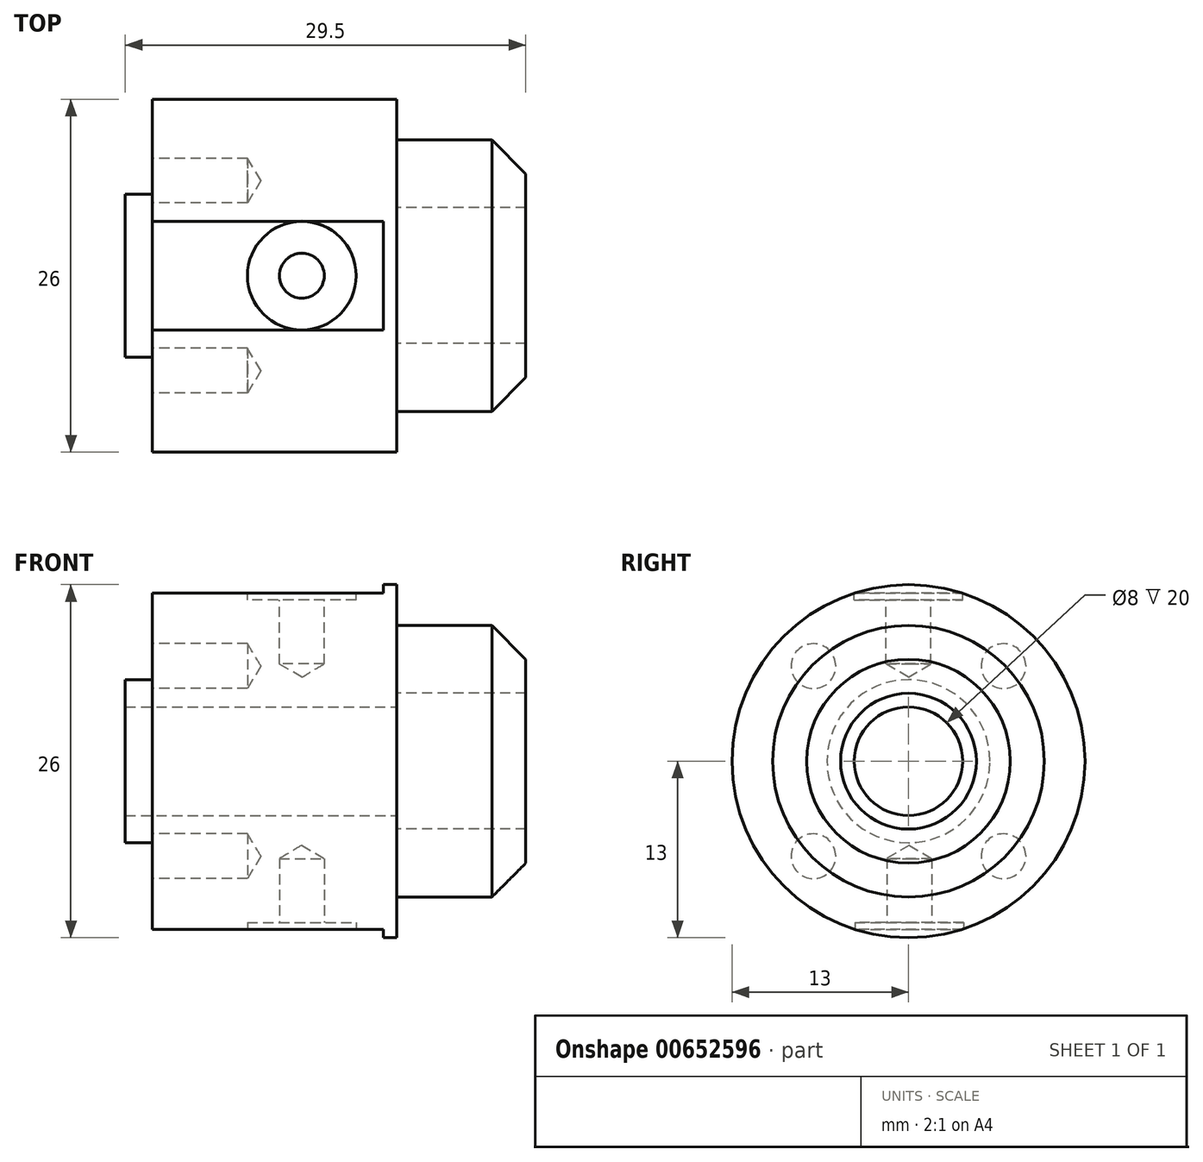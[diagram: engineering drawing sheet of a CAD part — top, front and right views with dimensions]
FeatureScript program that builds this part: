
annotation { "Feature Type Name" : "Feature", "Feature Type Description" : "" }
export const myFeature = defineFeature(function(context is Context, id is Id, definition is map)
    precondition{}
    {
        {
            var Q0;
            Q0=qCreatedBy(makeId("Front.planeOp"),FACE);
            var sketch = newSketch(context, id + "F0", { "sketchPlane" : qUnion([Q0])});
            skLineSegment(sketch, "E0", {"start": v(0, 4) * mm, "end": v(0, 13) * mm});
            skLineSegment(sketch, "E1", {"start": v(0, 13) * mm, "end": v(-18, 13) * mm});
            skLineSegment(sketch, "E2", {"start": v(-18, 13) * mm, "end": v(-18, 6) * mm});
            skLineSegment(sketch, "E3", {"start": v(-18, 6) * mm, "end": v(-20, 6) * mm});
            skLineSegment(sketch, "E4", {"start": v(-20, 6) * mm, "end": v(-20, 4) * mm});
            skPoint(sketch, "E5.startSnap0", {"position": v(0, 6.5) * mm});
            skLineSegment(sketch, "E6", {"start": v(0, 4) * mm, "end": v(-20, 4) * mm});
            skPoint(sketch, "E7.end.orphan", {"position": v(0, 0) * mm});
            skPoint(sketch, "E8.orphan", {"position": v(-20, 0) * mm});
            skLineSegment(sketch, "E9", {"start": v(0, 0) * mm, "end": v(-15.28, 0) * mm, "construction": true});
            skSolve(sketch);
        }
        {
            var Q0;
            Q0 = qSketchRegion(id + "F0", true);
            var Q1;
            Q1=sQuery(id+"F0.wireOp",EDGE,"E9");
            revolve(context, id + "F1", {"entities" : qUnion([Q0]), "axis" : qUnion([Q1]), "revolveType" : RevolveType.FULL});
        }
        {
            var Q0;
            Q0=makeQuery(id+"F1.opRevolve","SWEPT_FACE",FACE,{"disambiguationData":[OSD([sQuery(id+"F0.wireOp",EDGE,"E2")])]});
            var sketch = newSketch(context, id + "F2", { "sketchPlane" : qUnion([Q0])});
            skCircle(sketch, "E10", {"center": v(7, 7) * mm, "radius": 1.5 * mm});
            skCircle(sketch, "E11.1.0", {"center": v(-7, 7) * mm, "radius": 1.5 * mm});
            skCircle(sketch, "E11.2.0", {"center": v(-7, -7) * mm, "radius": 1.5 * mm});
            skCircle(sketch, "E11.3.0", {"center": v(7, -7) * mm, "radius": 1.5 * mm});
            skPoint(sketch, "E11.center", {"position": v(0, 0) * mm});
            skSolve(sketch);
        }
        {
            var Q0;
            Q0=sQuery(id+"F2.wireOp",VERTEX,"E11.1.0.center");
            var Q1;
            Q1=sQuery(id+"F2.wireOp",VERTEX,"E10.center");
            var Q2;
            Q2=sQuery(id+"F2.wireOp",VERTEX,"E11.2.0.center");
            var Q3;
            Q3=sQuery(id+"F2.wireOp",VERTEX,"E11.3.0.center");
            var Q4;
            Q4=makeQuery(id+"F1.opRevolve","SWEPT_BODY",BODY,{"disambiguationData":[OSD([sQuery(id+"F0.wireOp",EDGE,"E0"),sQuery(id+"F0.wireOp",EDGE,"E1"),sQuery(id+"F0.wireOp",EDGE,"E2"),sQuery(id+"F0.wireOp",EDGE,"E3"),sQuery(id+"F0.wireOp",EDGE,"E4"),sQuery(id+"F0.wireOp",EDGE,"E6")])]});
            hole(context, id + "F3", {"style" : HoleStyle.SIMPLE, "endStyle" : HoleEndStyle.BLIND, "standardTappedOrClearance" : lookupTablePath({ "standard" : "ISO", "engagement" : "75%", "pitch" : "0.7 mm", "size" : "M4", "type" : "Tapped" }), "standardBlindInLast" : lookupTablePath({ "standard" : "ISO", "engagement" : "75%", "pitch" : "0.7 mm", "size" : "M4", "type" : "Tapped" }), "holeDiameter" : 3.3 * mm, "majorDiameter" : 4 * mm, "showTappedDepth" : true, "holeDepth" : 7 * mm, "isTappedThrough" : true, "tappedDepth" : 7 * mm, "tapClearance" : 0, "locations" : qUnion([Q0, Q1, Q2, Q3]), "scope" : qUnion([Q4])});
        }
        {
            var Q0;
            Q0=makeQuery(id+"F1.opRevolve","SWEPT_FACE",FACE,{"disambiguationData":[OSD([sQuery(id+"F0.wireOp",EDGE,"E0")])]});
            var sketch = newSketch(context, id + "F4", { "sketchPlane" : qUnion([Q0])});
            skCircle(sketch, "E12", {"center": v(0, 0) * mm, "radius": 5 * mm});
            skCircle(sketch, "E13", {"center": v(0, 0) * mm, "radius": 10 * mm});
            skSolve(sketch);
        }
        {
            var Q0;
            Q0 = qSketchRegion(id + "F4", true);
            extrude(context, id + "F5", {"entities" : qUnion([Q0]), "operationType" : NewBodyOperationType.ADD, "depth" : 9.5 * mm, "offsetDistance" : 25 * mm});
        }
        {
            var Q0;
            Q0=makeQuery(id+"F5.opExtrude","CAP_EDGE",EDGE,{"disambiguationData":[OSD([sQuery(id+"F4.wireOp",EDGE,"E13")])],"isStart":false});
            chamfer(context, id + "F6", {"entities" : qUnion([Q0]), "width" : 2.5 * mm, "tangentPropagation" : true});
        }
        {
            var Q0;
            Q0=makeQuery(id+"F1.opRevolve","SWEPT_FACE",FACE,{"disambiguationData":[OSD([sQuery(id+"F0.wireOp",EDGE,"E2")])]});
            var sketch = newSketch(context, id + "F7", { "sketchPlane" : qUnion([Q0])});
            skArc(sketch, "E14", {"start": v(4, 12.37) * mm, "mid": v(0, 13) * mm, "end": v(-4, 12.37) * mm});
            skLineSegment(sketch, "E15", {"start": v(-4, 12.37) * mm, "end": v(4, 12.37) * mm});
            skLineSegment(sketch, "E16", {"start": v(-4, -12.37) * mm, "end": v(4, -12.37) * mm});
            skArc(sketch, "E17.trimOffspring", {"start": v(-4, -12.37) * mm, "mid": v(0, -13) * mm, "end": v(4, -12.37) * mm});
            skSolve(sketch);
        }
        {
            var Q0;
            Q0 = qSketchRegion(id + "F7", true);
            extrude(context, id + "F8", {"entities" : qUnion([Q0]), "operationType" : NewBodyOperationType.REMOVE, "oppositeDirection" : true, "depth" : 17 * mm, "offsetDistance" : 25 * mm});
        }
        {
            var Q0;
            Q0=makeQuery(id+"F8.boolean.opBoolean","COPY",FACE,{"derivedFrom":makeQuery(id+"F8.opExtrude","SWEPT_FACE",FACE,{"disambiguationData":[OSD([sQuery(id+"F7.wireOp",EDGE,"E15")])]})});
            var sketch = newSketch(context, id + "F9", { "sketchPlane" : qUnion([Q0])});
            skCircle(sketch, "E18", {"center": v(-7, 0) * mm, "radius": 2.97 * mm});
            skSolve(sketch);
        }
        {
            var Q0;
            Q0=sQuery(id+"F9.wireOp",VERTEX,"E18.center");
            var Q1;
            Q1=makeQuery(id+"F1.opRevolve","SWEPT_BODY",BODY,{"disambiguationData":[OSD([sQuery(id+"F0.wireOp",EDGE,"E0"),sQuery(id+"F0.wireOp",EDGE,"E1"),sQuery(id+"F0.wireOp",EDGE,"E2"),sQuery(id+"F0.wireOp",EDGE,"E3"),sQuery(id+"F0.wireOp",EDGE,"E4"),sQuery(id+"F0.wireOp",EDGE,"E6")])]});
            hole(context, id + "F10", {"style" : HoleStyle.SIMPLE, "endStyle" : HoleEndStyle.BLIND, "standardTappedOrClearance" : lookupTablePath({ "standard" : "ISO", "engagement" : "75%", "pitch" : "0.7 mm", "size" : "M4", "type" : "Tapped" }), "standardBlindInLast" : lookupTablePath({ "standard" : "ISO", "engagement" : "75%", "pitch" : "0.7 mm", "size" : "M4", "type" : "Tapped" }), "holeDiameter" : 3.3 * mm, "majorDiameter" : 4 * mm, "showTappedDepth" : true, "holeDepth" : 5.2 * mm, "isTappedThrough" : true, "tappedDepth" : 4.5 * mm, "tapClearance" : 1, "locations" : qUnion([Q0]), "scope" : qUnion([Q1])});
        }
        {
            var Q0;
            Q0=makeQuery(id+"F8.boolean.opBoolean","COPY",FACE,{"derivedFrom":makeQuery(id+"F8.opExtrude","SWEPT_FACE",FACE,{"disambiguationData":[OSD([sQuery(id+"F7.wireOp",EDGE,"E15")])]})});
            var sketch = newSketch(context, id + "F11", { "sketchPlane" : qUnion([Q0])});
            skCircle(sketch, "E19", {"center": v(-7, 0) * mm, "radius": 4 * mm});
            skSolve(sketch);
        }
        {
            var Q0;
            Q0 = qSketchRegion(id + "F11", true);
            extrude(context, id + "F12", {"entities" : qUnion([Q0]), "operationType" : NewBodyOperationType.REMOVE, "oppositeDirection" : true, "depth" : 0.5 * mm, "offsetDistance" : 25 * mm});
        }
        {
            var Q0;
            Q0=makeQuery(id+"F8.boolean.opBoolean","COPY",FACE,{"derivedFrom":makeQuery(id+"F8.opExtrude","SWEPT_FACE",FACE,{"disambiguationData":[OSD([sQuery(id+"F7.wireOp",EDGE,"E16")])]})});
            var sketch = newSketch(context, id + "F13", { "sketchPlane" : qUnion([Q0])});
            skCircle(sketch, "E20", {"center": v(-7, -0.05) * mm, "radius": 3.25 * mm});
            skSolve(sketch);
        }
        {
            var Q0;
            Q0=sQuery(id+"F13.wireOp",VERTEX,"E20.center");
            var Q1;
            Q1=makeQuery(id+"F1.opRevolve","SWEPT_BODY",BODY,{"disambiguationData":[OSD([sQuery(id+"F0.wireOp",EDGE,"E0"),sQuery(id+"F0.wireOp",EDGE,"E1"),sQuery(id+"F0.wireOp",EDGE,"E2"),sQuery(id+"F0.wireOp",EDGE,"E3"),sQuery(id+"F0.wireOp",EDGE,"E4"),sQuery(id+"F0.wireOp",EDGE,"E6")])]});
            hole(context, id + "F14", {"style" : HoleStyle.SIMPLE, "endStyle" : HoleEndStyle.BLIND, "standardTappedOrClearance" : lookupTablePath({ "standard" : "ISO", "engagement" : "75%", "pitch" : "0.7 mm", "size" : "M4", "type" : "Tapped" }), "standardBlindInLast" : lookupTablePath({ "standard" : "ISO", "engagement" : "75%", "pitch" : "0.7 mm", "size" : "M4", "type" : "Tapped" }), "holeDiameter" : 3.3 * mm, "majorDiameter" : 4 * mm, "showTappedDepth" : true, "holeDepth" : 5.2 * mm, "isTappedThrough" : true, "tappedDepth" : 4.5 * mm, "tapClearance" : 1, "locations" : qUnion([Q0]), "scope" : qUnion([Q1])});
        }
        {
            var Q0;
            Q0=makeQuery(id+"F8.boolean.opBoolean","COPY",FACE,{"derivedFrom":makeQuery(id+"F8.opExtrude","SWEPT_FACE",FACE,{"disambiguationData":[OSD([sQuery(id+"F7.wireOp",EDGE,"E16")])]})});
            var sketch = newSketch(context, id + "F15", { "sketchPlane" : qUnion([Q0])});
            skCircle(sketch, "E21", {"center": v(-7, -0.05) * mm, "radius": 4 * mm});
            skSolve(sketch);
        }
        {
            var Q0;
            Q0 = qSketchRegion(id + "F15", true);
            extrude(context, id + "F16", {"entities" : qUnion([Q0]), "operationType" : NewBodyOperationType.REMOVE, "oppositeDirection" : true, "depth" : 0.5 * mm, "offsetDistance" : 25 * mm});
        }
    });
